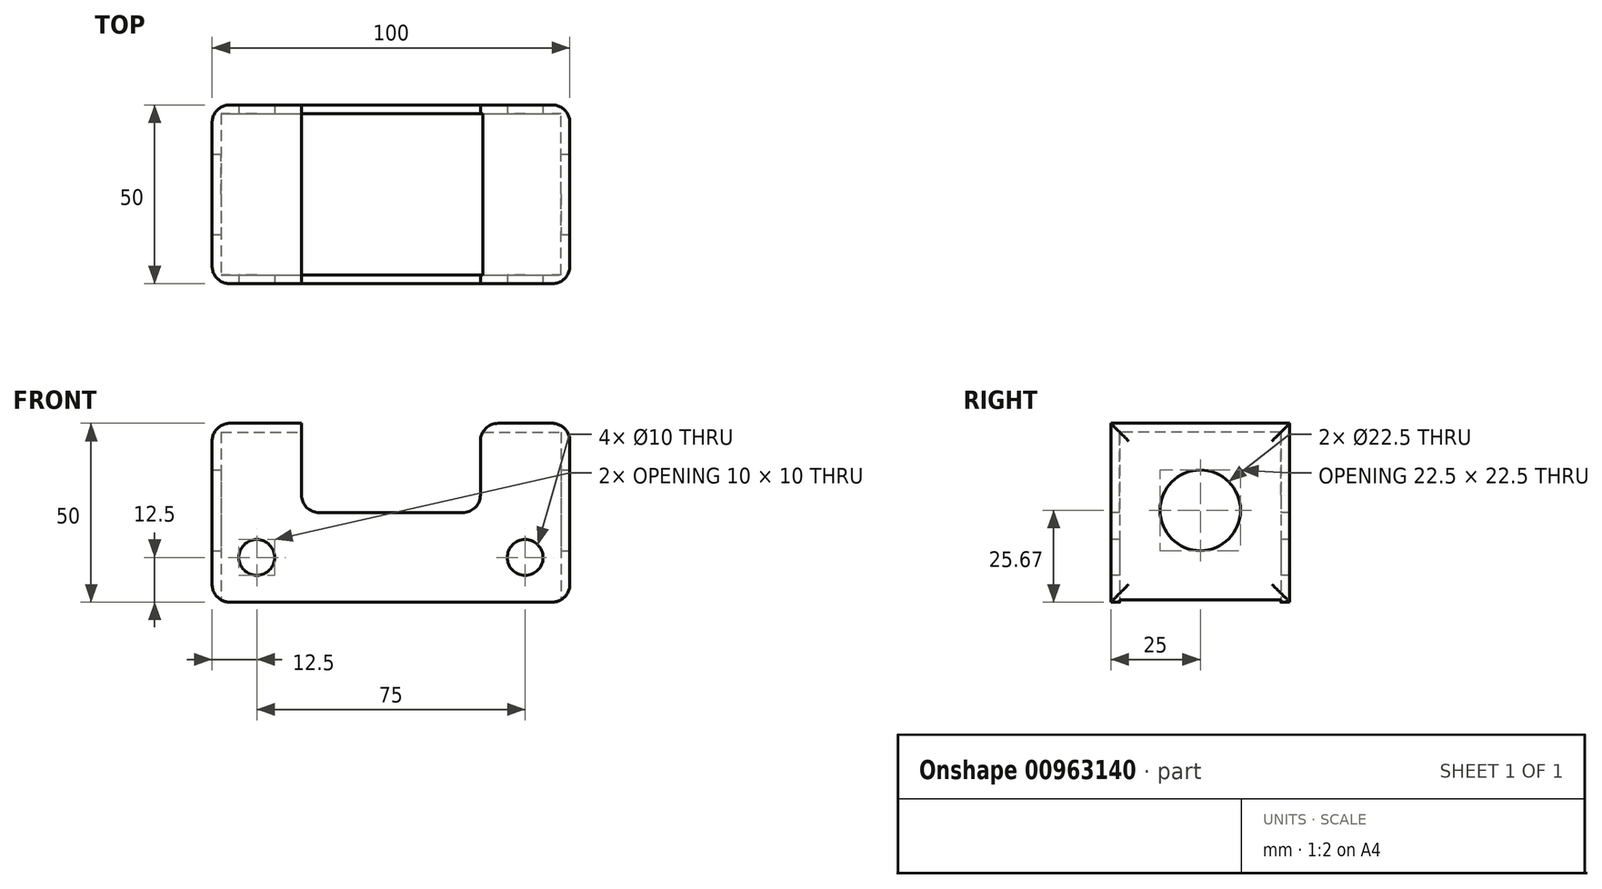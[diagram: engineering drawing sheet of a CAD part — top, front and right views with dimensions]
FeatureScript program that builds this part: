
annotation { "Feature Type Name" : "Feature", "Feature Type Description" : "" }
export const myFeature = defineFeature(function(context is Context, id is Id, definition is map)
    precondition{}
    {
        {
            var Q0;
            Q0=qCreatedBy(makeId("Top.planeOp"),FACE);
            var sketch = newSketch(context, id + "F0", { "sketchPlane" : qUnion([Q0])});
            skLineSegment(sketch, "E0.bottom", {"start": v(0, 0) * mm, "end": v(100, 0) * mm});
            skLineSegment(sketch, "E0.top", {"start": v(0, 50) * mm, "end": v(100, 50) * mm});
            skLineSegment(sketch, "E0.left", {"start": v(0, 0) * mm, "end": v(0, 50) * mm});
            skLineSegment(sketch, "E0.right", {"start": v(100, 0) * mm, "end": v(100, 50) * mm});
            skSolve(sketch);
        }
        {
            var Q0;
            Q0 = qSketchRegion(id + "F0", true);
            extrude(context, id + "F1", {"entities" : qUnion([Q0]), "depth" : 50 * mm, "offsetDistance" : 25 * mm});
        }
        {
            var Q0;
            Q0=makeQuery(id+"F1.opExtrude","CAP_FACE",FACE,{"disambiguationData":[OSD([sQuery(id+"F0.wireOp",EDGE,"E0.bottom"),sQuery(id+"F0.wireOp",EDGE,"E0.top"),sQuery(id+"F0.wireOp",EDGE,"E0.left"),sQuery(id+"F0.wireOp",EDGE,"E0.right")])],"isStart":true});
            shell(context, id + "F2", {"entities" : qUnion([Q0]), "thickness" : 2.5 * mm});
        }
        {
            var Q0;
            Q0=makeQuery(id+"F1.opExtrude","CAP_FACE",FACE,{"disambiguationData":[OSD([sQuery(id+"F0.wireOp",EDGE,"E0.bottom"),sQuery(id+"F0.wireOp",EDGE,"E0.top"),sQuery(id+"F0.wireOp",EDGE,"E0.left"),sQuery(id+"F0.wireOp",EDGE,"E0.right")])],"isStart":false});
            var sketch = newSketch(context, id + "F3", { "sketchPlane" : qUnion([Q0])});
            skLineSegment(sketch, "E1.bottom", {"start": v(25, 60.14) * mm, "end": v(75, 60.14) * mm});
            skLineSegment(sketch, "E1.top", {"start": v(25, -10.14) * mm, "end": v(75, -10.14) * mm});
            skLineSegment(sketch, "E1.left", {"start": v(25, 60.14) * mm, "end": v(25, -10.14) * mm});
            skLineSegment(sketch, "E1.right", {"start": v(75, 60.14) * mm, "end": v(75, -10.14) * mm});
            skSolve(sketch);
        }
        {
            var Q0;
            Q0 = qSketchRegion(id + "F3", true);
            extrude(context, id + "F4", {"entities" : qUnion([Q0]), "operationType" : NewBodyOperationType.REMOVE, "oppositeDirection" : true, "depth" : 25 * mm, "offsetDistance" : 25 * mm});
        }
        {
            var Q0;
            Q0=makeQuery(id+"F1.opExtrude","SWEPT_FACE",FACE,{"disambiguationData":[OSD([sQuery(id+"F0.wireOp",EDGE,"E0.bottom")])]});
            var sketch = newSketch(context, id + "F5", { "sketchPlane" : qUnion([Q0])});
            skCircle(sketch, "E2", {"center": v(12.5, 12.5) * mm, "radius": 5 * mm});
            skCircle(sketch, "E3", {"center": v(87.5, 12.5) * mm, "radius": 5 * mm});
            skSolve(sketch);
        }
        {
            var Q0;
            Q0 = qSketchRegion(id + "F5", true);
            extrude(context, id + "F6", {"entities" : qUnion([Q0]), "operationType" : NewBodyOperationType.REMOVE, "oppositeDirection" : true, "depth" : 50 * mm, "offsetDistance" : 25 * mm});
        }
        {
            var Q0;
            Q0=makeQuery(id+"F1.opExtrude","CAP_EDGE",EDGE,{"disambiguationData":[OSD([sQuery(id+"F0.wireOp",EDGE,"E0.left")])],"isStart":false});
            var Q1;
            Q1=makeQuery(id+"F1.opExtrude","CAP_EDGE",EDGE,{"disambiguationData":[OSD([sQuery(id+"F0.wireOp",EDGE,"E0.left")])],"isStart":true});
            var Q2;
            Q2=makeQuery(id+"F1.opExtrude","SWEPT_EDGE",EDGE,{"disambiguationData":[OSD([sQuery(id+"F0.wireOp",EDGE,"E0.bottom"),sQuery(id+"F0.wireOp",EDGE,"E0.left")])]});
            var Q3;
            Q3=makeQuery(id+"F1.opExtrude","SWEPT_EDGE",EDGE,{"disambiguationData":[OSD([sQuery(id+"F0.wireOp",EDGE,"E0.top"),sQuery(id+"F0.wireOp",EDGE,"E0.left")])]});
            fillet(context, id + "F7", {"entities" : qUnion([Q0, Q1, Q2, Q3]), "radius" : 5 * mm, "tangentPropagation" : true, "allowEdgeOverflow" : false});
        }
        {
            var Q0;
            Q0=makeQuery(id+"F4.boolean.opBoolean","COPY",EDGE,{"derivedFrom":makeQuery(id+"F4.opExtrude","CAP_EDGE",EDGE,{"disambiguationData":[OSD([sQuery(id+"F3.wireOp",EDGE,"E1.left")])],"isStart":true})});
            var Q1;
            Q1=makeQuery(id+"F4.boolean.opBoolean","COPY",EDGE,{"derivedFrom":makeQuery(id+"F4.opExtrude","CAP_EDGE",EDGE,{"disambiguationData":[OSD([sQuery(id+"F3.wireOp",EDGE,"E1.right")])],"isStart":true})});
            var Q2;
            {var subQ0=sQuery(id+"F0.wireOp",EDGE,"E0.bottom");var subQ1=sQuery(id+"F3.wireOp",EDGE,"E1.left");Q2=makeQuery(id+"F4.boolean.opBoolean","COPY",EDGE,{"disambiguationData":[TD([makeQuery(id+"F1.opExtrude","SWEPT_FACE",FACE,{"disambiguationData":[OSD([subQ0])]})])],"derivedFrom":makeQuery(id+"F4.opExtrude","CAP_EDGE",EDGE,{"disambiguationData":[OSD([subQ1])],"isStart":false})});}
            var Q3;
            {var subQ0=sQuery(id+"F0.wireOp",EDGE,"E0.top");var subQ1=sQuery(id+"F3.wireOp",EDGE,"E1.left");Q3=makeQuery(id+"F4.boolean.opBoolean","COPY",EDGE,{"disambiguationData":[TD([makeQuery(id+"F1.opExtrude","SWEPT_FACE",FACE,{"disambiguationData":[OSD([subQ0])]})])],"derivedFrom":makeQuery(id+"F4.opExtrude","CAP_EDGE",EDGE,{"disambiguationData":[OSD([subQ1])],"isStart":false})});}
            var Q4;
            {var subQ0=sQuery(id+"F0.wireOp",EDGE,"E0.top");var subQ1=sQuery(id+"F3.wireOp",EDGE,"E1.right");Q4=makeQuery(id+"F4.boolean.opBoolean","COPY",EDGE,{"disambiguationData":[TD([makeQuery(id+"F1.opExtrude","SWEPT_FACE",FACE,{"disambiguationData":[OSD([subQ0])]})])],"derivedFrom":makeQuery(id+"F4.opExtrude","CAP_EDGE",EDGE,{"disambiguationData":[OSD([subQ1])],"isStart":false})});}
            var Q5;
            {var subQ0=sQuery(id+"F0.wireOp",EDGE,"E0.bottom");var subQ1=sQuery(id+"F3.wireOp",EDGE,"E1.right");Q5=makeQuery(id+"F4.boolean.opBoolean","COPY",EDGE,{"disambiguationData":[TD([makeQuery(id+"F1.opExtrude","SWEPT_FACE",FACE,{"disambiguationData":[OSD([subQ0])]})])],"derivedFrom":makeQuery(id+"F4.opExtrude","CAP_EDGE",EDGE,{"disambiguationData":[OSD([subQ1])],"isStart":false})});}
            fillet(context, id + "F8", {"entities" : qUnion([Q0, Q1, Q2, Q3, Q4, Q5]), "radius" : 5 * mm, "tangentPropagation" : true, "allowEdgeOverflow" : false});
        }
        {
            var Q0;
            Q0=makeQuery(id+"F1.opExtrude","CAP_EDGE",EDGE,{"disambiguationData":[OSD([sQuery(id+"F0.wireOp",EDGE,"E0.right")])],"isStart":false});
            var Q1;
            Q1=makeQuery(id+"F1.opExtrude","CAP_EDGE",EDGE,{"disambiguationData":[OSD([sQuery(id+"F0.wireOp",EDGE,"E0.right")])],"isStart":true});
            var Q2;
            Q2=makeQuery(id+"F1.opExtrude","SWEPT_EDGE",EDGE,{"disambiguationData":[OSD([sQuery(id+"F0.wireOp",EDGE,"E0.bottom"),sQuery(id+"F0.wireOp",EDGE,"E0.right")])]});
            var Q3;
            Q3=makeQuery(id+"F1.opExtrude","SWEPT_EDGE",EDGE,{"disambiguationData":[OSD([sQuery(id+"F0.wireOp",EDGE,"E0.top"),sQuery(id+"F0.wireOp",EDGE,"E0.right")])]});
            fillet(context, id + "F9", {"entities" : qUnion([Q0, Q1, Q2, Q3]), "radius" : 5 * mm, "tangentPropagation" : true, "allowEdgeOverflow" : false});
        }
        {
            var Q0;
            Q0=makeQuery(id+"F1.opExtrude","SWEPT_FACE",FACE,{"disambiguationData":[OSD([sQuery(id+"F0.wireOp",EDGE,"E0.right")])]});
            var sketch = newSketch(context, id + "F10", { "sketchPlane" : qUnion([Q0])});
            skCircle(sketch, "E4", {"center": v(25, 25.67) * mm, "radius": 11.25 * mm});
            skSolve(sketch);
        }
        {
            var Q0;
            Q0 = qSketchRegion(id + "F10", true);
            extrude(context, id + "F11", {"entities" : qUnion([Q0]), "operationType" : NewBodyOperationType.REMOVE, "oppositeDirection" : true, "depth" : 100 * mm, "offsetDistance" : 25 * mm});
        }
    });
